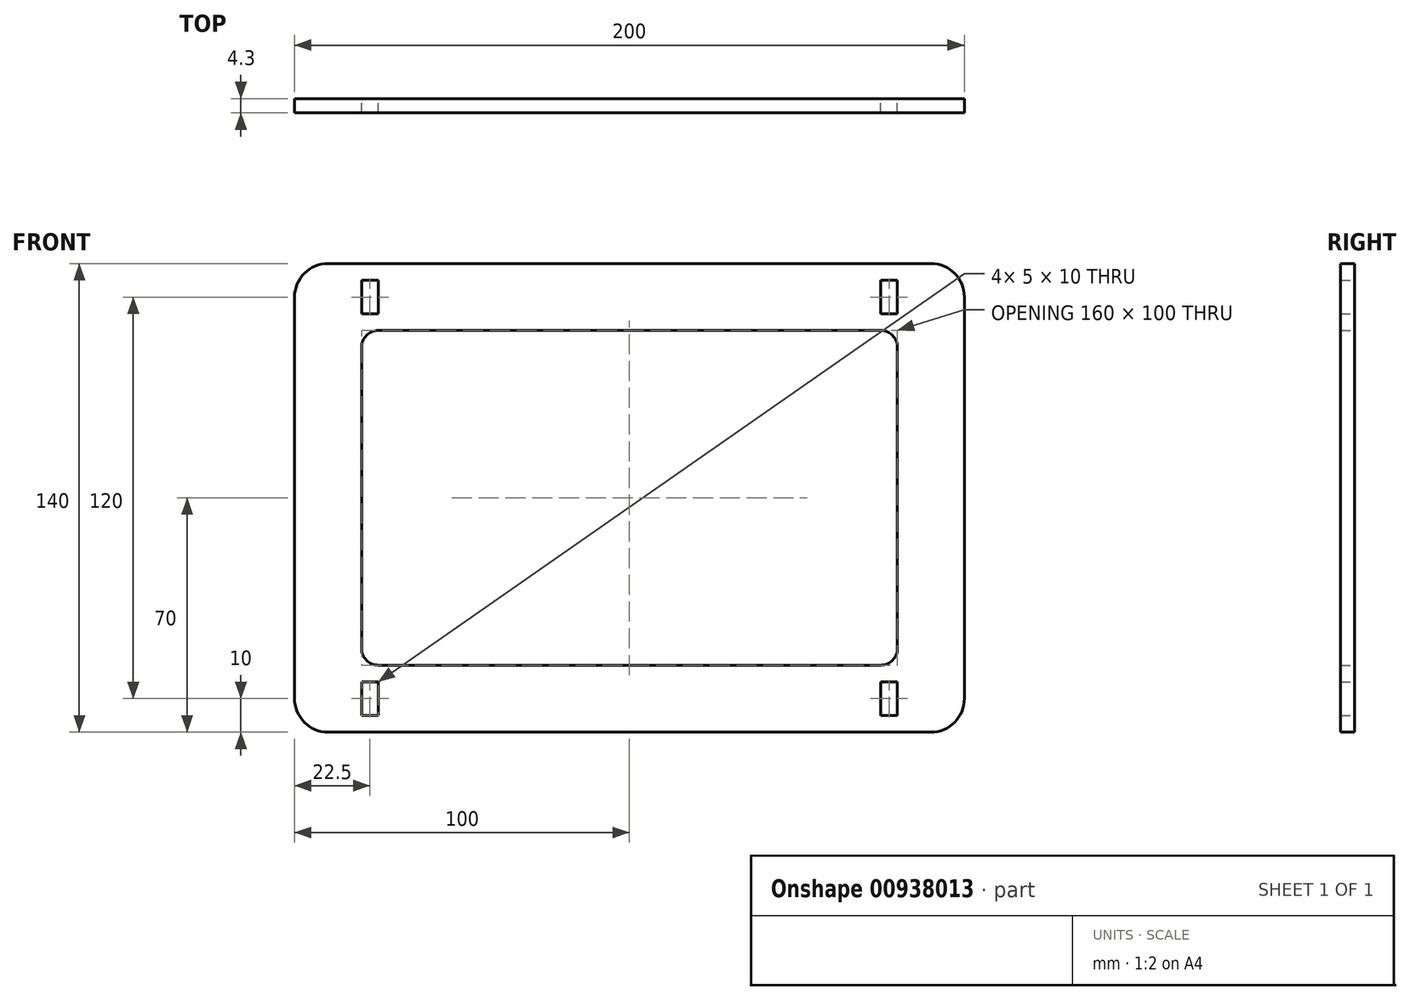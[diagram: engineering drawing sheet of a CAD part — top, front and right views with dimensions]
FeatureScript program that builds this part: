
annotation { "Feature Type Name" : "Feature", "Feature Type Description" : "" }
export const myFeature = defineFeature(function(context is Context, id is Id, definition is map)
    precondition{}
    {
        {
            var Q0;
            Q0=qCreatedBy(makeId("Front.planeOp"),FACE);
            var sketch = newSketch(context, id + "F0", { "sketchPlane" : qUnion([Q0])});
            skLineSegment(sketch, "E0.bottom", {"start": v(-90, 70) * mm, "end": v(90, 70) * mm});
            skLineSegment(sketch, "E0.top", {"start": v(-90, -70) * mm, "end": v(90, -70) * mm});
            skLineSegment(sketch, "E0.left", {"start": v(-100, 60) * mm, "end": v(-100, -60) * mm});
            skLineSegment(sketch, "E0.right", {"start": v(100, 60) * mm, "end": v(100, -60) * mm});
            skPoint(sketch, "E0.middle", {"position": v(0, 0) * mm});
            skLineSegment(sketch, "E1.bottom", {"start": v(-75, 50) * mm, "end": v(75, 50) * mm});
            skLineSegment(sketch, "E1.top", {"start": v(-75, -50) * mm, "end": v(75, -50) * mm});
            skLineSegment(sketch, "E1.left", {"start": v(-80, 45) * mm, "end": v(-80, -45) * mm});
            skLineSegment(sketch, "E1.right", {"start": v(80, 45) * mm, "end": v(80, -45) * mm});
            skLineSegment(sketch, "E2.bottom", {"start": v(-80, 65) * mm, "end": v(-75, 65) * mm});
            skLineSegment(sketch, "E2.top", {"start": v(-80, 55) * mm, "end": v(-75, 55) * mm});
            skLineSegment(sketch, "E2.left", {"start": v(-80, 65) * mm, "end": v(-80, 55) * mm});
            skLineSegment(sketch, "E2.right", {"start": v(-75, 65) * mm, "end": v(-75, 55) * mm});
            skLineSegment(sketch, "E3.MirrorCS", {"start": v(80, 65) * mm, "end": v(75, 65) * mm});
            skLineSegment(sketch, "E4.MirrorCS", {"start": v(75, 65) * mm, "end": v(75, 55) * mm});
            skLineSegment(sketch, "E5.MirrorCS", {"start": v(80, 55) * mm, "end": v(75, 55) * mm});
            skLineSegment(sketch, "E6.MirrorCS", {"start": v(80, 65) * mm, "end": v(80, 55) * mm});
            skLineSegment(sketch, "E7.MirrorCS", {"start": v(-80, -65) * mm, "end": v(-75, -65) * mm});
            skLineSegment(sketch, "E8.MirrorCS", {"start": v(-80, -65) * mm, "end": v(-80, -55) * mm});
            skLineSegment(sketch, "E9.MirrorCS", {"start": v(-80, -55) * mm, "end": v(-75, -55) * mm});
            skLineSegment(sketch, "E10.MirrorCS", {"start": v(-75, -65) * mm, "end": v(-75, -55) * mm});
            skLineSegment(sketch, "E11.MirrorCS", {"start": v(80, -55) * mm, "end": v(75, -55) * mm});
            skLineSegment(sketch, "E12.MirrorCS", {"start": v(80, -65) * mm, "end": v(80, -55) * mm});
            skLineSegment(sketch, "E13.MirrorCS", {"start": v(80, -65) * mm, "end": v(75, -65) * mm});
            skLineSegment(sketch, "E14.MirrorCS", {"start": v(75, -65) * mm, "end": v(75, -55) * mm});
            skPoint(sketch, "E15.visualSharp", {"position": v(-100, 70) * mm});
            skArc(sketch, "E15.filletArc", {"start": v(-90, 70) * mm, "mid": v(-97.07, 67.07) * mm, "end": v(-100, 60) * mm});
            skPoint(sketch, "E16.visualSharp", {"position": v(100, 70) * mm});
            skArc(sketch, "E16.filletArc", {"start": v(100, 60) * mm, "mid": v(97.07, 67.07) * mm, "end": v(90, 70) * mm});
            skPoint(sketch, "E17.visualSharp", {"position": v(100, -70) * mm});
            skArc(sketch, "E17.filletArc", {"start": v(90, -70) * mm, "mid": v(97.07, -67.07) * mm, "end": v(100, -60) * mm});
            skPoint(sketch, "E18.visualSharp", {"position": v(-100, -70) * mm});
            skArc(sketch, "E18.filletArc", {"start": v(-100, -60) * mm, "mid": v(-97.07, -67.07) * mm, "end": v(-90, -70) * mm});
            skPoint(sketch, "E19.visualSharp", {"position": v(-80, 50) * mm});
            skArc(sketch, "E19.filletArc", {"start": v(-75, 50) * mm, "mid": v(-78.54, 48.54) * mm, "end": v(-80, 45) * mm});
            skPoint(sketch, "E20.visualSharp", {"position": v(80, 50) * mm});
            skArc(sketch, "E20.filletArc", {"start": v(80, 45) * mm, "mid": v(78.54, 48.54) * mm, "end": v(75, 50) * mm});
            skPoint(sketch, "E21.visualSharp", {"position": v(80, -50) * mm});
            skArc(sketch, "E21.filletArc", {"start": v(75, -50) * mm, "mid": v(78.54, -48.54) * mm, "end": v(80, -45) * mm});
            skPoint(sketch, "E22.visualSharp", {"position": v(-80, -50) * mm});
            skArc(sketch, "E22.filletArc", {"start": v(-80, -45) * mm, "mid": v(-78.54, -48.54) * mm, "end": v(-75, -50) * mm});
            skSolve(sketch);
        }
        {
            var Q0;
            Q0 = qSketchRegion(id + "F0", true);
            extrude(context, id + "F1", {"entities" : qUnion([Q0]), "depth" : 4.3 * mm, "offsetDistance" : 25 * mm});
        }
    });
